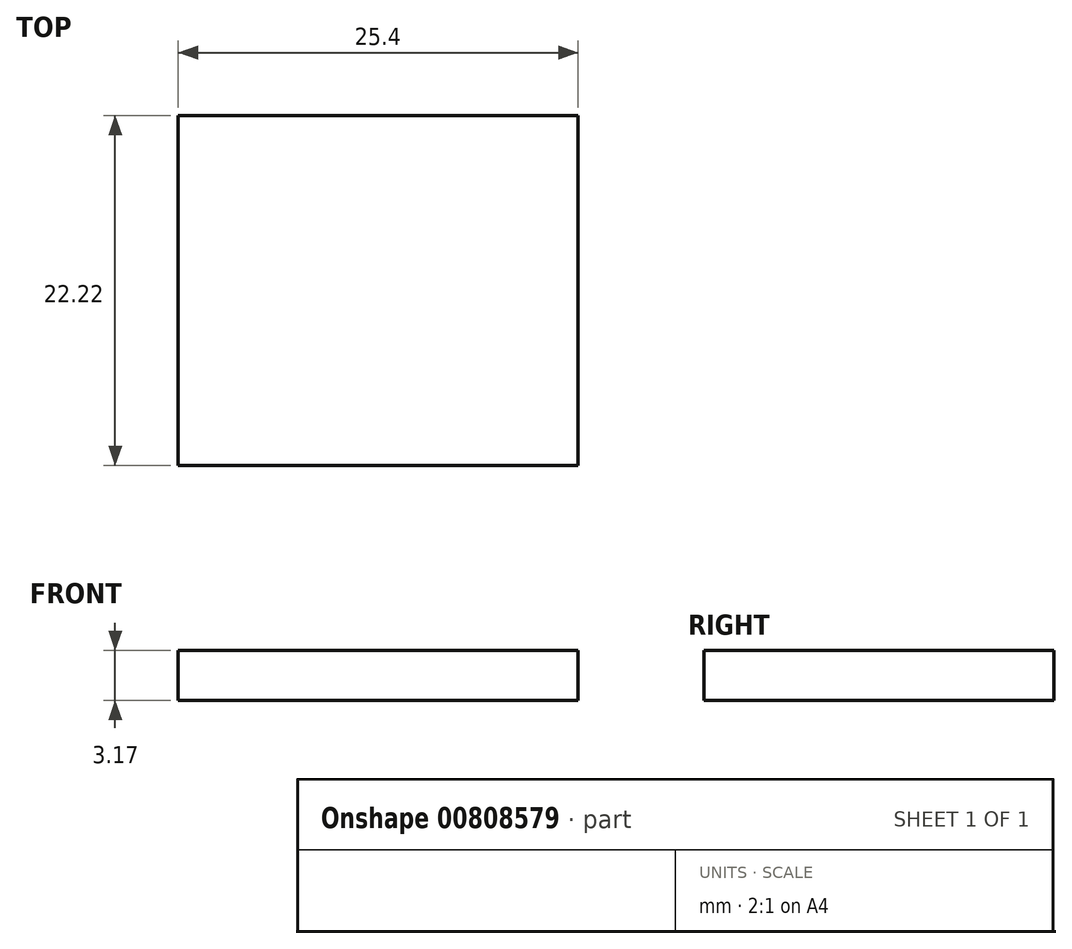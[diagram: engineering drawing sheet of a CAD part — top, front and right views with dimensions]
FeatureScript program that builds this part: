
annotation { "Feature Type Name" : "Feature", "Feature Type Description" : "" }
export const myFeature = defineFeature(function(context is Context, id is Id, definition is map)
    precondition{}
    {
        {
            var Q0;
            Q0=qCreatedBy(makeId("Top.planeOp"),FACE);
            var sketch = newSketch(context, id + "F0", { "sketchPlane" : qUnion([Q0])});
            skLineSegment(sketch, "E0.bottom", {"start": v(-42.48, 11.88) * mm, "end": v(-17.08, 11.88) * mm});
            skLineSegment(sketch, "E0.top", {"start": v(-42.48, -10.34) * mm, "end": v(-17.08, -10.34) * mm});
            skLineSegment(sketch, "E0.left", {"start": v(-42.48, 11.88) * mm, "end": v(-42.48, -10.34) * mm});
            skLineSegment(sketch, "E0.right", {"start": v(-17.08, 11.88) * mm, "end": v(-17.08, -10.34) * mm});
            skSolve(sketch);
        }
        {
            var Q0;
            Q0=makeQuery(id+"F0.imprint","IMPRINT",FACE,{"disambiguationData":[TD([[makeQuery(id+"F0.imprint","IMPRINT",EDGE,{"derivedFrom":sQuery(id+"F0.wireOp",EDGE,"E0.bottom")}),-1.0]])]});
            extrude(context, id + "F1", {"entities" : qUnion([Q0]), "depth" : 3.17 * mm, "offsetDistance" : 25.4 * mm});
        }
    });
